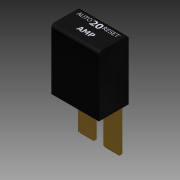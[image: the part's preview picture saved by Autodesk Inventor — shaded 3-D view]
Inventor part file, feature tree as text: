
AUTODESK INVENTOR PART (.ipt)
format: ipt  version: 2013 (Build 170138000, 138)  size: 449,024 bytes
history: native  units: in
note: dims shown in document units (in); Inventor stores cm internally (conversion verified against a paired STEP export)
features: sketch x6, extrude x4, plane x3, emboss x2, fillet x1, mirror x1
ambient origin geometry x8: Origin, YZ Plane, XZ Plane, XY Plane, X Axis, Y Axis, Z Axis, Center Point
bodies: Solid1 (feature_tree)
feature tree (17):
  extrude  "Extrusion1"  Depth=0.39in
  fillet  "Fillet1"  Radius=0.78in
  extrude  "Extrusion3"  Depth=0.212in
  extrude  "Extrusion4"  Depth=0.0585in
  extrude  "Extrusion5"  Depth=0.57in TaperAngle=0.0deg
  plane  "Work Plane1"
  mirror  "Mirror1"
  plane  "Work Plane2"
  emboss  "Emboss1"
  plane  "Work Plane4"
  emboss  "Emboss3"
  sketch  "Sketch1"  dims[d0=0.62in d1=0.39in d2=0.78in d3=0.0in]
  sketch  "Sketch2"  dims[d4=0.01in d5=0.05in d6=0.212in]
  sketch  "Sketch3"  dims[d8=0.031in d13=0.0585in]
  sketch  "Sketch4"  dims[d14=0.57in d15=0.0in d16=0.57in d17=0.0in]
  sketch  "Sketch6"  dims[d18=0.023in]
  sketch  "Sketch8"  dims[d19=0.023in d20=0.023in d21=0.57in d22=0.0in d26=0.1875in d27=0.0001in d28=0.0in d32=0.1875in d33=0.0001in d34=0.0in]
